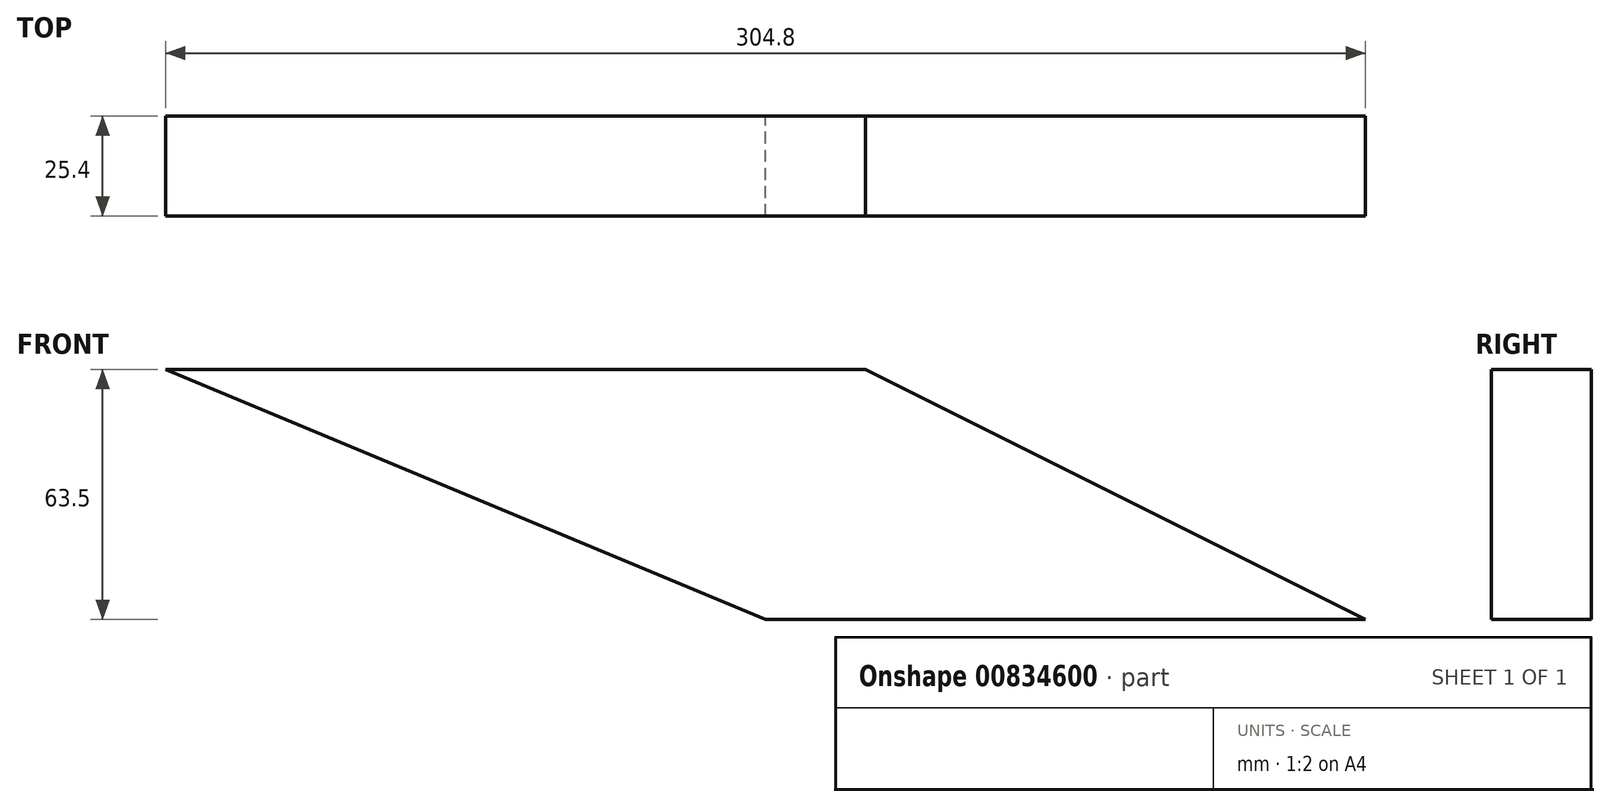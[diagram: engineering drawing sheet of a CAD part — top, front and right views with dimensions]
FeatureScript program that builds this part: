
annotation { "Feature Type Name" : "Feature", "Feature Type Description" : "" }
export const myFeature = defineFeature(function(context is Context, id is Id, definition is map)
    precondition{}
    {
        {
            var Q0;
            Q0=qCreatedBy(makeId("Front.planeOp"),FACE);
            var sketch = newSketch(context, id + "F0", { "sketchPlane" : qUnion([Q0])});
            skLineSegment(sketch, "E0", {"start": v(-12.7, 0) * mm, "end": v(139.7, 0) * mm});
            skLineSegment(sketch, "E1", {"start": v(139.7, 0) * mm, "end": v(12.7, 63.5) * mm});
            skLineSegment(sketch, "E2", {"start": v(12.7, 63.5) * mm, "end": v(-165.1, 63.5) * mm});
            skLineSegment(sketch, "E3", {"start": v(-165.1, 63.5) * mm, "end": v(-12.7, 0) * mm});
            skSolve(sketch);
        }
        {
            var Q0;
            Q0=makeQuery(id+"F0.imprint","IMPRINT",FACE,{"disambiguationData":[TD([[makeQuery(id+"F0.imprint","IMPRINT",EDGE,{"derivedFrom":sQuery(id+"F0.wireOp",EDGE,"E0")}),1.0]])]});
            extrude(context, id + "F1", {"entities" : qUnion([Q0]), "depth" : 25.4 * mm, "offsetDistance" : 25.4 * mm});
        }
    });
